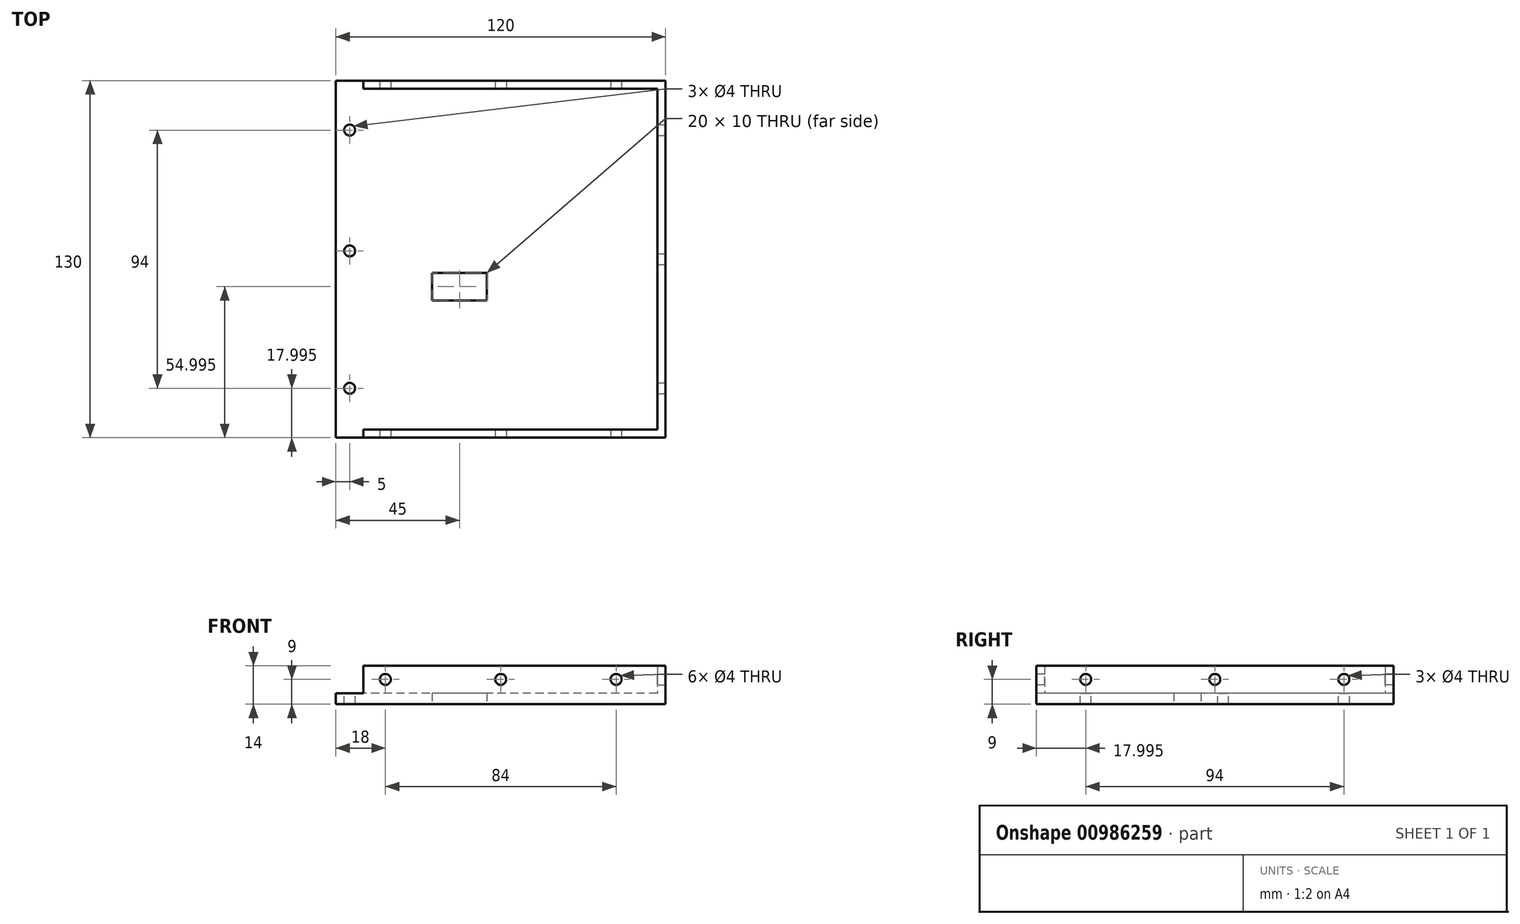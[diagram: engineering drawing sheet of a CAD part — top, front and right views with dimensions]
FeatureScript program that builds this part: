
annotation { "Feature Type Name" : "Feature", "Feature Type Description" : "" }
export const myFeature = defineFeature(function(context is Context, id is Id, definition is map)
    precondition{}
    {
        {
            var Q0;
            Q0=qCreatedBy(makeId("Top.planeOp"),FACE);
            var sketch = newSketch(context, id + "F0", { "sketchPlane" : qUnion([Q0])});
            skLineSegment(sketch, "E0.top", {"start": v(-97.73, -89) * mm, "end": v(22.27, -89) * mm});
            skLineSegment(sketch, "E0.left", {"start": v(-97.73, 41) * mm, "end": v(-97.73, -89) * mm});
            skLineSegment(sketch, "E0.right", {"start": v(22.27, 41) * mm, "end": v(22.27, -89) * mm});
            skLineSegment(sketch, "E1", {"start": v(-97.73, 41) * mm, "end": v(22.27, 41) * mm});
            skSolve(sketch);
        }
        {
            var Q0;
            Q0=qSketchRegion(id+"F0",true);
            extrude(context, id + "F1", {"entities" : qUnion([Q0]), "depth" : 4 * mm, "offsetDistance" : 25 * mm});
        }
        {
            var Q0;
            Q0=makeQuery(id+"F1.opExtrude","CAP_FACE",FACE,{"disambiguationData":[OSD([sQuery(id+"F0.wireOp",EDGE,"E0.top"),sQuery(id+"F0.wireOp",EDGE,"E0.left"),sQuery(id+"F0.wireOp",EDGE,"E0.right"),sQuery(id+"F0.wireOp",EDGE,"E1")])],"isStart":false});
            var sketch = newSketch(context, id + "F2", { "sketchPlane" : qUnion([Q0])});
            skLineSegment(sketch, "E2", {"start": v(-87.73, -89) * mm, "end": v(22.27, -89) * mm});
            skLineSegment(sketch, "E3", {"start": v(22.27, -89) * mm, "end": v(22.27, 41) * mm});
            skLineSegment(sketch, "E4", {"start": v(22.27, 41) * mm, "end": v(-87.73, 41) * mm});
            skLineSegment(sketch, "E5", {"start": v(-87.73, 41) * mm, "end": v(-87.73, 38) * mm});
            skLineSegment(sketch, "E6", {"start": v(-87.73, 38) * mm, "end": v(19.27, 38) * mm});
            skLineSegment(sketch, "E7", {"start": v(19.27, 38) * mm, "end": v(19.27, -86) * mm});
            skLineSegment(sketch, "E8", {"start": v(19.27, -86) * mm, "end": v(-87.73, -86) * mm});
            skLineSegment(sketch, "E9", {"start": v(-87.73, -86) * mm, "end": v(-87.73, -89) * mm});
            skSolve(sketch);
        }
        {
            var Q0;
            Q0 = qSketchRegion(id + "F2", true);
            extrude(context, id + "F3", {"entities" : qUnion([Q0]), "operationType" : NewBodyOperationType.ADD, "depth" : 10 * mm, "offsetDistance" : 25 * mm});
        }
        {
            var Q0;
            Q0=makeQuery(id+"F1.opExtrude","CAP_FACE",FACE,{"disambiguationData":[OSD([sQuery(id+"F0.wireOp",EDGE,"E0.top"),sQuery(id+"F0.wireOp",EDGE,"E0.left"),sQuery(id+"F0.wireOp",EDGE,"E0.right"),sQuery(id+"F0.wireOp",EDGE,"E1")])],"isStart":false});
            var sketch = newSketch(context, id + "F4", { "sketchPlane" : qUnion([Q0])});
            skCircle(sketch, "E10", {"center": v(-92.73, -21) * mm, "radius": 2 * mm});
            skCircle(sketch, "E11", {"center": v(-92.73, -71) * mm, "radius": 2 * mm});
            skCircle(sketch, "E12", {"center": v(-92.73, 23) * mm, "radius": 2 * mm});
            skSolve(sketch);
        }
        {
            var Q0;
            Q0 = qSketchRegion(id + "F4", true);
            extrude(context, id + "F5", {"entities" : qUnion([Q0]), "operationType" : NewBodyOperationType.REMOVE, "oppositeDirection" : true, "depth" : 5 * mm, "offsetDistance" : 25 * mm});
        }
        {
            var Q0;
            Q0=makeQuery(id+"F3.boolean.opBoolean","MERGE",FACE,{"derivedFrom":[makeQuery(id+"F1.opExtrude","SWEPT_FACE",FACE,{"disambiguationData":[OSD([sQuery(id+"F0.wireOp",EDGE,"E0.top")])]}),makeQuery(id+"F3.opExtrude","SWEPT_FACE",FACE,{"disambiguationData":[OSD([sQuery(id+"F2.wireOp",EDGE,"E2")])]})]});
            var sketch = newSketch(context, id + "F6", { "sketchPlane" : qUnion([Q0])});
            skCircle(sketch, "E13", {"center": v(4.27, 9) * mm, "radius": 2 * mm});
            skCircle(sketch, "E14", {"center": v(-37.73, 9) * mm, "radius": 2 * mm});
            skCircle(sketch, "E15", {"center": v(-79.73, 9) * mm, "radius": 2 * mm});
            skSolve(sketch);
        }
        {
            var Q0;
            Q0 = qSketchRegion(id + "F6", true);
            extrude(context, id + "F7", {"entities" : qUnion([Q0]), "operationType" : NewBodyOperationType.REMOVE, "oppositeDirection" : true, "depth" : 135 * mm, "offsetDistance" : 25 * mm});
        }
        {
            var Q0;
            Q0=makeQuery(id+"F3.boolean.opBoolean","MERGE",FACE,{"derivedFrom":[makeQuery(id+"F1.opExtrude","SWEPT_FACE",FACE,{"disambiguationData":[OSD([sQuery(id+"F0.wireOp",EDGE,"E0.right")])]}),makeQuery(id+"F3.opExtrude","SWEPT_FACE",FACE,{"disambiguationData":[OSD([sQuery(id+"F2.wireOp",EDGE,"E3")])]})]});
            var sketch = newSketch(context, id + "F8", { "sketchPlane" : qUnion([Q0])});
            skCircle(sketch, "E16", {"center": v(-71, 9) * mm, "radius": 2 * mm});
            skCircle(sketch, "E17", {"center": v(-24, 9) * mm, "radius": 2 * mm});
            skCircle(sketch, "E18", {"center": v(23, 9) * mm, "radius": 2 * mm});
            skPoint(sketch, "E18.centerSnap0", {"position": v(37.51, 9) * mm});
            skSolve(sketch);
        }
        {
            var Q0;
            Q0 = qSketchRegion(id + "F8", true);
            extrude(context, id + "F9", {"entities" : qUnion([Q0]), "operationType" : NewBodyOperationType.REMOVE, "oppositeDirection" : true, "depth" : 5 * mm, "offsetDistance" : 25 * mm});
        }
        {
            var Q0;
            Q0=makeQuery(id+"F0.imprint","IMPRINT",FACE,{"disambiguationData":[TD([[makeQuery(id+"F0.imprint","IMPRINT",EDGE,{"derivedFrom":sQuery(id+"F0.wireOp",EDGE,"E0.top")}),1.0]])]});
            var sketch = newSketch(context, id + "F10", { "sketchPlane" : qUnion([Q0])});
            skLineSegment(sketch, "E19.bottom", {"start": v(-62.73, -39) * mm, "end": v(-42.73, -39) * mm});
            skLineSegment(sketch, "E19.top", {"start": v(-62.73, -29) * mm, "end": v(-42.73, -29) * mm});
            skLineSegment(sketch, "E19.left", {"start": v(-62.73, -39) * mm, "end": v(-62.73, -29) * mm});
            skLineSegment(sketch, "E19.right", {"start": v(-42.73, -39) * mm, "end": v(-42.73, -29) * mm});
            skSolve(sketch);
        }
        {
            var Q0;
            Q0 = qSketchRegion(id + "F10", true);
            extrude(context, id + "F11", {"entities" : qUnion([Q0]), "operationType" : NewBodyOperationType.REMOVE, "depth" : 5 * mm, "offsetDistance" : 25 * mm});
        }
    });
